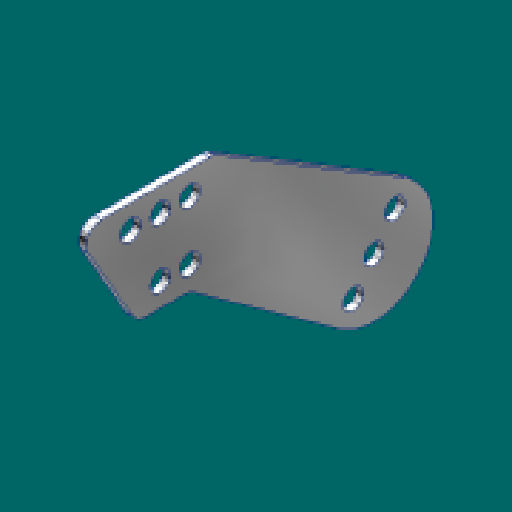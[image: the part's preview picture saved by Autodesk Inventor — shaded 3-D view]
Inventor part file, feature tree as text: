
AUTODESK INVENTOR PART (.ipt)
format: ipt  version: 2023.1 (Build 271208000, 208)  size: 144,384 bytes
history: native  units: in
note: dims shown in document units (in); Inventor stores cm internally (conversion verified against a paired STEP export)
features: extrude x1, fillet x1, sketch x1
ambient origin geometry x8: Origin, YZ Plane, XZ Plane, XY Plane, X Axis, Y Axis, Z Axis, Center Point
bodies: Solid1 (feature_tree)
feature tree (3):
  extrude  "Extrusion1"  Depth=0.125in
  fillet  "Fillet1"  Radius=0.45in
  sketch  "Sketch1"  dims[d0=0.17in d1=1.56in d2=0.45in d3=0.505in d5=1.0in d6=0.9in d7=0.65in d8=0.17in d9=0.2in d10=0.2in d11=0.5in d12=0.5in d13=0.7874in d15=0.25in d16=0.7874in d18=0.5in d21=30.0deg d22=0.25in d23=0.0625in d24=0.0in d25=0.125in d26=0.17in d29=0.6in d30=0.7874in d32=360.0deg]
